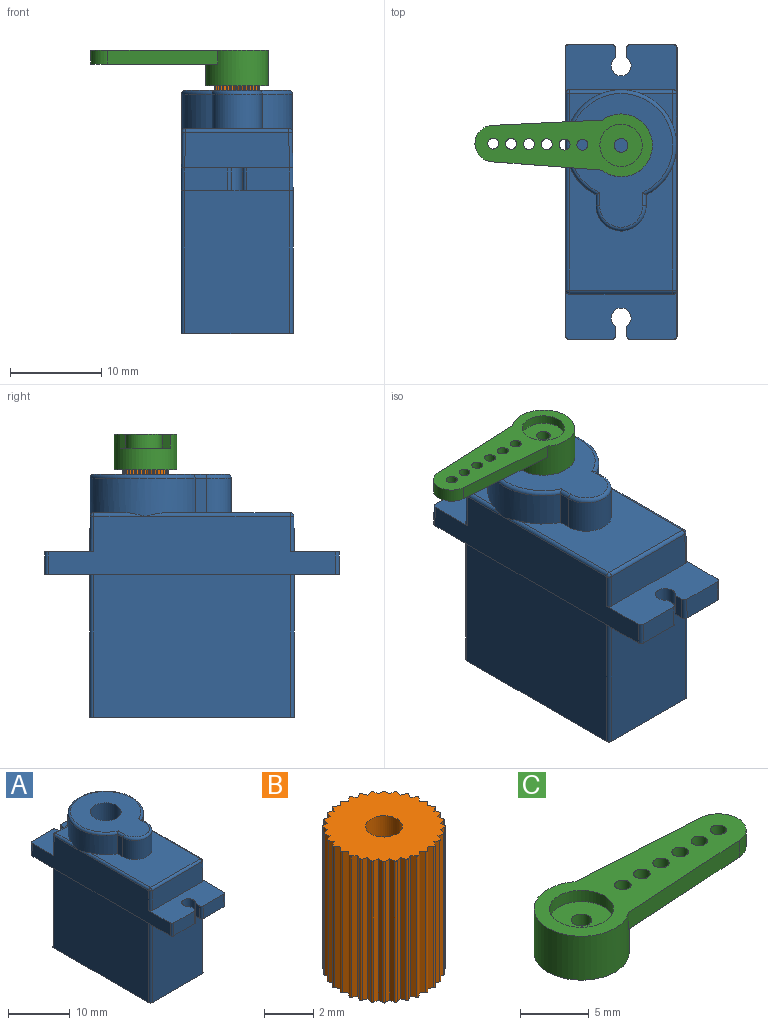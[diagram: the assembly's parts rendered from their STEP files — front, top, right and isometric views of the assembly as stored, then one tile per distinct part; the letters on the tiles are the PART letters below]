
ASSEMBLY  parts=3 mates=2
PART A: 64 faces, bbox 13.2x32.4x26.7 mm
  f0: plane 3.52x3.52mm, normal (0,0,1), area 4.4mm2, adj f4,f7,f57
  f1: plane 3.52x3.52mm, normal (0,0,1), area 4.4mm2, adj f5,f8,f57
  f2: plane 13.72x11.39mm, normal (0,0,1), area 107.7mm2, adj f3,f6,f47,f53,f54,f57,f58
  f3: cylinder r=0.4mm len=15.89mm, axis (0,1,0), area 9.3mm2, adj f2,f17,f45,f57
  f4: cylinder r=0.4mm len=5.69mm, axis (0,1,0), area 2.9mm2, adj f0,f17,f50,f57
  f5: cylinder r=0.4mm len=5.69mm, axis (0,1,0), area 2.9mm2, adj f1,f15,f51,f57
  f6: cylinder r=0.4mm len=15.89mm, axis (0,1,0), area 9.3mm2, adj f2,f15,f49,f57
  f7: cylinder r=0.4mm len=5.69mm, axis (-1,0,0), area 2.9mm2, adj f0,f16,f50,f57
  f8: cylinder r=0.4mm len=5.69mm, axis (-1,0,0), area 2.9mm2, adj f1,f16,f51,f57
  f9: plane 4.73x2.5mm, normal (0,1,0.01), area 11.8mm2, adj f11,f12,f32,f36
  f10: plane 4.73x2.5mm, normal (0,1,0.01), area 11.8mm2, adj f11,f12,f33,f37
  f11: plane 12.3x5.35mm, normal (0,0,-1), area 55.4mm2, adj f9,f10,f15,f17,f22,f29,f30,f31
  f12: plane 12.26x5.35mm, normal (0,0,1), area 55.2mm2, adj f9,f10,f15,f16,f17,f29,f30,f31
  f13: plane 4.73x2.5mm, normal (0,-1,0.01), area 11.8mm2, adj f14,f25,f34,f38
  f14: plane 12.26x5.35mm, normal (0,0,1), area 55.2mm2, adj f13,f15,f17,f18,f24,f26,f27,f28
  f15: plane 31.6x6.4mm, normal (1,0,0.01), area 163.4mm2, adj f5,f6,f11,f12,f14,f23,f25,f36
  f16: plane 11.46x3.9mm, normal (0,1,0.01), area 44.6mm2, adj f7,f8,f12,f48,f52
  f17: plane 31.6x6.4mm, normal (-1,0,0.01), area 163.4mm2, adj f3,f4,f11,f12,f14,f21,f25,f37
  f18: plane 11.46x3.9mm, normal (0,-1,0.01), area 44.6mm2, adj f14,f44,f46,f47
  f19: plane 22.5x12.3mm, normal (0,0,-1), area 276.6mm2, adj f20,f21,f22,f23,f40,f41,f42,f43
  f20: plane 15.7x11.5mm, normal (0,-1,0), area 180.5mm2, adj f19,f25,f42,f43
  f21: plane 21.7x15.7mm, normal (-1,0,0), area 340.7mm2, adj f17,f19,f41,f42
  f22: plane 15.7x11.5mm, normal (0,1,0), area 180.5mm2, adj f11,f19,f40,f41
  f23: plane 21.7x15.7mm, normal (1,0,0), area 340.7mm2, adj f15,f19,f40,f43
  f24: plane 4.73x2.5mm, normal (0,-1,0.01), area 11.8mm2, adj f14,f25,f35,f39
  f25: plane 12.3x5.35mm, normal (0,0,-1), area 55.4mm2, adj f13,f15,f17,f20,f24,f26,f27,f28
  f26: cylinder r=1.1mm len=2.5mm, axis (0,0,1), area 14mm2, adj f14,f25,f27,f28
  f27: plane 2.5x1.04mm, normal (1,0,0), area 2.6mm2, adj f14,f25,f26,f34
  f28: plane 2.5x1.04mm, normal (-1,0,0), area 2.6mm2, adj f14,f25,f26,f35
  f29: plane 2.5x1.04mm, normal (-1,0,0), area 2.6mm2, adj f11,f12,f31,f32
  f30: plane 2.5x1.04mm, normal (1,0,0), area 2.6mm2, adj f11,f12,f31,f33
  f31: cylinder r=1.1mm len=2.5mm, axis (0,0,1), area 14mm2, adj f11,f12,f29,f30
  f32: cylinder r=0.4mm len=2.51mm, axis (0,0.01,-1), area 1.6mm2, adj f9,f11,f12,f29
  f33: cylinder r=0.4mm len=2.51mm, axis (0,-0.01,1), area 1.6mm2, adj f10,f11,f12,f30
  f34: cylinder r=0.4mm len=2.51mm, axis (0,0.01,1), area 1.6mm2, adj f13,f14,f25,f27
  f35: cylinder r=0.4mm len=2.51mm, axis (0,-0.01,-1), area 1.6mm2, adj f14,f24,f25,f28
  f36: cylinder r=0.4mm len=2.5mm, axis (0.01,0.01,-1), area 1.6mm2, adj f9,f11,f12,f15
  f37: cylinder r=0.4mm len=2.5mm, axis (-0.01,0.01,-1), area 1.6mm2, adj f10,f11,f12,f17
  f38: cylinder r=0.4mm len=2.5mm, axis (-0.01,-0.01,-1), area 1.6mm2, adj f13,f14,f17,f25
  f39: cylinder r=0.4mm len=2.5mm, axis (0.01,-0.01,-1), area 1.6mm2, adj f14,f15,f24,f25
  f40: cylinder r=0.4mm len=15.7mm, axis (0,0,-1), area 9.9mm2, adj f11,f19,f22,f23
  f41: cylinder r=0.4mm len=15.7mm, axis (0,0,1), area 9.9mm2, adj f11,f19,f21,f22
  f42: cylinder r=0.4mm len=15.7mm, axis (0,0,-1), area 9.9mm2, adj f19,f20,f21,f25
  f43: cylinder r=0.4mm len=15.7mm, axis (0,0,1), area 9.9mm2, adj f19,f20,f23,f25
  f44: cylinder r=0.4mm len=3.91mm, axis (-0.01,-0.01,-1), area 2.5mm2, adj f14,f17,f18,f45
  f45: sphere r=0.4mm, area 0.2mm2, adj f3,f44,f47
  f46: cylinder r=0.4mm len=3.91mm, axis (0.01,-0.01,-1), area 2.5mm2, adj f14,f15,f18,f49
  f47: cylinder r=0.4mm len=11.39mm, axis (-1,0,0), area 7.1mm2, adj f2,f18,f45,f49
  f48: cylinder r=0.4mm len=3.91mm, axis (-0.01,0.01,-1), area 2.5mm2, adj f12,f16,f17,f50
  f49: sphere r=0.4mm, area 0.2mm2, adj f6,f46,f47
  f50: sphere r=0.4mm, area 0.2mm2, adj f4,f7,f48
  f51: sphere r=0.4mm, area 0.2mm2, adj f5,f8,f52
  f52: cylinder r=0.4mm len=3.91mm, axis (0.01,0.01,-1), area 2.5mm2, adj f12,f15,f16,f51
  f53: plane 3.8x1.22mm, normal (-1,0,0), area 4.6mm2, adj f2,f54,f57,f61
  f54: cylinder r=2.75mm len=5.5mm, axis (0,0,-1), area 32.8mm2, adj f2,f53,f58,f63
  f55: plane 14.7x11.39mm, normal (0,0,1), area 96.2mm2, adj f56,f60,f61,f62,f63
  f56: cylinder r=2.5mm len=5mm, axis (0,0,-1), area 66mm2, adj f55,f59
  f57: cylinder r=6.09mm len=12.19mm, axis (0,0,-1), area 125.9mm2, adj f0,f1,f2,f3,f4,f5,f6,f7
  f58: plane 3.8x1.22mm, normal (1,0,0), area 4.6mm2, adj f2,f54,f57,f62
  f59: plane 5x5mm, normal (0,0,1), area 19.6mm2, adj f56
  f60: torus R=5.69mm, axis (0,0,1), area 20.1mm2, adj f55,f57,f61,f62
  f61: cylinder r=0.4mm len=1.47mm, axis (0,1,0), area 0.8mm2, adj f53,f55,f60,f63
  f62: cylinder r=0.4mm len=1.47mm, axis (0,-1,0), area 0.8mm2, adj f55,f58,f60,f63
  f63: torus R=2.35mm, axis (0,0,1), area 5.1mm2, adj f54,f55,f61,f62
PART B: 99 faces, bbox 5x5x7.1 mm
  f0: plane 5x5mm, normal (0,0,-1), area 16.5mm2, adj f1,f2,f3,f4,f5,f6,f7,f8
  f1: plane 7.05x0.2mm, normal (-0.8,0.6,0), area 1.7mm2, adj f0,f2,f94,f95
  f2: cylinder r=0.08mm len=7.05mm, axis (0,0,-1), area 0.9mm2, adj f0,f1,f3,f94
  f3: plane 7.05x0.21mm, normal (-0.51,-0.86,0), area 1.7mm2, adj f0,f2,f4,f94
  f4: plane 7.05x0.22mm, normal (-0.9,0.43,0), area 1.7mm2, adj f0,f3,f5,f94
  f5: cylinder r=0.08mm len=7.05mm, axis (0,0,-1), area 0.9mm2, adj f0,f4,f6,f94
  f6: plane 7.05x0.23mm, normal (-0.33,-0.94,0), area 1.7mm2, adj f0,f5,f7,f94
  f7: plane 7.05x0.24mm, normal (-0.97,0.25,0), area 1.7mm2, adj f0,f6,f8,f94
  f8: cylinder r=0.08mm len=7.05mm, axis (0,0,-1), area 0.9mm2, adj f0,f7,f9,f94
  f9: plane 7.05x0.25mm, normal (-0.14,-0.99,0), area 1.7mm2, adj f0,f8,f10,f94
  f10: plane 7.05x0.25mm, normal (-1,0.05,0), area 1.7mm2, adj f0,f9,f11,f94
  f11: cylinder r=0.08mm len=7.05mm, axis (0,0,-1), area 0.9mm2, adj f0,f10,f12,f94
  f12: plane 7.05x0.25mm, normal (0.05,-1,0), area 1.7mm2, adj f0,f11,f13,f94
  f13: plane 7.05x0.25mm, normal (-0.99,-0.14,0), area 1.7mm2, adj f0,f12,f14,f94
  f14: cylinder r=0.08mm len=7.05mm, axis (0,0,-1), area 0.9mm2, adj f0,f13,f15,f94
  f15: plane 7.05x0.24mm, normal (0.25,-0.97,0), area 1.7mm2, adj f0,f14,f16,f94
  f16: plane 7.05x0.23mm, normal (-0.94,-0.33,0), area 1.7mm2, adj f0,f15,f17,f94
  f17: cylinder r=0.08mm len=7.05mm, axis (0,0,-1), area 0.9mm2, adj f0,f16,f18,f94
  f18: plane 7.05x0.22mm, normal (0.43,-0.9,0), area 1.7mm2, adj f0,f17,f19,f94
  f19: plane 7.05x0.21mm, normal (-0.86,-0.51,0), area 1.7mm2, adj f0,f18,f20,f94
  f20: cylinder r=0.08mm len=7.05mm, axis (0,0,-1), area 0.9mm2, adj f0,f19,f21,f94
  f21: plane 7.05x0.2mm, normal (0.6,-0.8,0), area 1.7mm2, adj f0,f20,f22,f94
  f22: plane 7.05x0.18mm, normal (-0.74,-0.67,0), area 1.7mm2, adj f0,f21,f23,f94
  f23: cylinder r=0.08mm len=7.05mm, axis (0,0,-1), area 0.9mm2, adj f0,f22,f24,f94
  f24: plane 7.05x0.18mm, normal (0.74,-0.67,0), area 1.7mm2, adj f0,f23,f25,f94
  f25: plane 7.05x0.2mm, normal (-0.6,-0.8,0), area 1.7mm2, adj f0,f24,f26,f94
  f26: cylinder r=0.08mm len=7.05mm, axis (0,0,-1), area 0.9mm2, adj f0,f25,f27,f94
  f27: plane 7.05x0.21mm, normal (0.86,-0.51,0), area 1.7mm2, adj f0,f26,f28,f94
  f28: plane 7.05x0.22mm, normal (-0.43,-0.9,0), area 1.7mm2, adj f0,f27,f29,f94
  f29: cylinder r=0.08mm len=7.05mm, axis (0,0,-1), area 0.9mm2, adj f0,f28,f30,f94
  f30: plane 7.05x0.23mm, normal (0.94,-0.33,0), area 1.7mm2, adj f0,f29,f31,f94
  f31: plane 7.05x0.24mm, normal (-0.25,-0.97,0), area 1.7mm2, adj f0,f30,f32,f94
  f32: cylinder r=0.08mm len=7.05mm, axis (0,0,-1), area 0.9mm2, adj f0,f31,f33,f94
  f33: plane 7.05x0.25mm, normal (0.99,-0.14,0), area 1.7mm2, adj f0,f32,f34,f94
  f34: plane 7.05x0.25mm, normal (-0.05,-1,0), area 1.7mm2, adj f0,f33,f35,f94
  f35: cylinder r=0.08mm len=7.05mm, axis (0,0,-1), area 0.9mm2, adj f0,f34,f36,f94
  f36: plane 7.05x0.25mm, normal (1,0.05,0), area 1.7mm2, adj f0,f35,f37,f94
  f37: plane 7.05x0.25mm, normal (0.14,-0.99,0), area 1.7mm2, adj f0,f36,f38,f94
  f38: cylinder r=0.08mm len=7.05mm, axis (0,0,-1), area 0.9mm2, adj f0,f37,f39,f94
  f39: plane 7.05x0.24mm, normal (0.97,0.25,0), area 1.7mm2, adj f0,f38,f40,f94
  f40: plane 7.05x0.23mm, normal (0.33,-0.94,0), area 1.7mm2, adj f0,f39,f41,f94
  f41: cylinder r=0.08mm len=7.05mm, axis (0,0,-1), area 0.9mm2, adj f0,f40,f42,f94
  f42: plane 7.05x0.22mm, normal (0.9,0.43,0), area 1.7mm2, adj f0,f41,f43,f94
  f43: plane 7.05x0.21mm, normal (0.51,-0.86,0), area 1.7mm2, adj f0,f42,f44,f94
  f44: cylinder r=0.08mm len=7.05mm, axis (0,0,-1), area 0.9mm2, adj f0,f43,f45,f94
  f45: plane 7.05x0.2mm, normal (0.8,0.6,0), area 1.7mm2, adj f0,f44,f46,f94
  f46: plane 7.05x0.18mm, normal (0.67,-0.74,0), area 1.7mm2, adj f0,f45,f47,f94
  f47: cylinder r=0.08mm len=7.05mm, axis (0,0,-1), area 0.9mm2, adj f0,f46,f48,f94
  f48: plane 7.05x0.18mm, normal (0.67,0.74,0), area 1.7mm2, adj f0,f47,f49,f94
  f49: plane 7.05x0.2mm, normal (0.8,-0.6,0), area 1.7mm2, adj f0,f48,f50,f94
  f50: cylinder r=0.08mm len=7.05mm, axis (0,0,-1), area 0.9mm2, adj f0,f49,f51,f94
  f51: plane 7.05x0.21mm, normal (0.51,0.86,0), area 1.7mm2, adj f0,f50,f52,f94
  f52: plane 7.05x0.22mm, normal (0.9,-0.43,0), area 1.7mm2, adj f0,f51,f53,f94
  f53: cylinder r=0.08mm len=7.05mm, axis (0,0,-1), area 0.9mm2, adj f0,f52,f54,f94
  f54: plane 7.05x0.23mm, normal (0.33,0.94,0), area 1.7mm2, adj f0,f53,f55,f94
  f55: plane 7.05x0.24mm, normal (0.97,-0.25,0), area 1.7mm2, adj f0,f54,f56,f94
  f56: cylinder r=0.08mm len=7.05mm, axis (0,0,-1), area 0.9mm2, adj f0,f55,f57,f94
  f57: plane 7.05x0.25mm, normal (0.14,0.99,0), area 1.7mm2, adj f0,f56,f58,f94
  f58: plane 7.05x0.25mm, normal (1,-0.05,0), area 1.7mm2, adj f0,f57,f59,f94
  f59: cylinder r=0.08mm len=7.05mm, axis (0,0,-1), area 0.9mm2, adj f0,f58,f60,f94
  f60: plane 7.05x0.25mm, normal (-0.05,1,0), area 1.7mm2, adj f0,f59,f61,f94
  f61: plane 7.05x0.25mm, normal (0.99,0.14,0), area 1.7mm2, adj f0,f60,f62,f94
  f62: cylinder r=0.08mm len=7.05mm, axis (0,0,-1), area 0.9mm2, adj f0,f61,f63,f94
  f63: plane 7.05x0.24mm, normal (-0.25,0.97,0), area 1.7mm2, adj f0,f62,f64,f94
  f64: plane 7.05x0.23mm, normal (0.94,0.33,0), area 1.7mm2, adj f0,f63,f65,f94
  f65: cylinder r=0.08mm len=7.05mm, axis (0,0,-1), area 0.9mm2, adj f0,f64,f66,f94
  f66: plane 7.05x0.22mm, normal (-0.43,0.9,0), area 1.7mm2, adj f0,f65,f67,f94
  f67: plane 7.05x0.21mm, normal (0.86,0.51,0), area 1.7mm2, adj f0,f66,f68,f94
  f68: cylinder r=0.08mm len=7.05mm, axis (0,0,-1), area 0.9mm2, adj f0,f67,f69,f94
  f69: plane 7.05x0.2mm, normal (-0.6,0.8,0), area 1.7mm2, adj f0,f68,f70,f94
  f70: plane 7.05x0.18mm, normal (0.74,0.67,0), area 1.7mm2, adj f0,f69,f71,f94
  f71: cylinder r=0.08mm len=7.05mm, axis (0,0,-1), area 0.9mm2, adj f0,f70,f72,f94
  f72: plane 7.05x0.18mm, normal (-0.74,0.67,0), area 1.7mm2, adj f0,f71,f73,f94
  f73: plane 7.05x0.2mm, normal (0.6,0.8,0), area 1.7mm2, adj f0,f72,f74,f94
  f74: cylinder r=0.08mm len=7.05mm, axis (0,0,-1), area 0.9mm2, adj f0,f73,f75,f94
  f75: plane 7.05x0.21mm, normal (-0.86,0.51,0), area 1.7mm2, adj f0,f74,f76,f94
  f76: plane 7.05x0.22mm, normal (0.43,0.9,0), area 1.7mm2, adj f0,f75,f77,f94
  f77: cylinder r=0.08mm len=7.05mm, axis (0,0,-1), area 0.9mm2, adj f0,f76,f78,f94
  f78: plane 7.05x0.23mm, normal (-0.94,0.33,0), area 1.7mm2, adj f0,f77,f79,f94
  f79: plane 7.05x0.24mm, normal (0.25,0.97,0), area 1.7mm2, adj f0,f78,f80,f94
  f80: cylinder r=0.08mm len=7.05mm, axis (0,0,-1), area 0.9mm2, adj f0,f79,f81,f94
  f81: plane 7.05x0.25mm, normal (-0.99,0.14,0), area 1.7mm2, adj f0,f80,f82,f94
  f82: plane 7.05x0.25mm, normal (0.05,1,0), area 1.7mm2, adj f0,f81,f83,f94
  f83: cylinder r=0.08mm len=7.05mm, axis (0,0,-1), area 0.9mm2, adj f0,f82,f84,f94
  f84: plane 7.05x0.25mm, normal (-1,-0.05,0), area 1.7mm2, adj f0,f83,f85,f94
  f85: plane 7.05x0.25mm, normal (-0.14,0.99,0), area 1.7mm2, adj f0,f84,f86,f94
  f86: cylinder r=0.08mm len=7.05mm, axis (0,0,-1), area 0.9mm2, adj f0,f85,f87,f94
  f87: plane 7.05x0.24mm, normal (-0.97,-0.25,0), area 1.7mm2, adj f0,f86,f88,f94
  f88: plane 7.05x0.23mm, normal (-0.33,0.94,0), area 1.7mm2, adj f0,f87,f89,f94
  f89: cylinder r=0.08mm len=7.05mm, axis (0,0,-1), area 0.9mm2, adj f0,f88,f90,f94
  f90: plane 7.05x0.22mm, normal (-0.9,-0.43,0), area 1.7mm2, adj f0,f89,f91,f94
  f91: plane 7.05x0.21mm, normal (-0.51,0.86,0), area 1.7mm2, adj f0,f90,f92,f94
  f92: cylinder r=0.08mm len=7.05mm, axis (0,0,-1), area 0.9mm2, adj f0,f91,f93,f94
  f93: plane 7.05x0.2mm, normal (-0.8,-0.6,0), area 1.7mm2, adj f0,f92,f94,f96
  f94: plane 5x5mm, normal (0,0,1), area 16.5mm2, adj f1,f2,f3,f4,f5,f6,f7,f8
  f95: plane 7.05x0.18mm, normal (-0.67,-0.74,0), area 1.7mm2, adj f0,f1,f94,f97
  f96: plane 7.05x0.18mm, normal (-0.67,0.74,0), area 1.7mm2, adj f0,f93,f94,f97
  f97: cylinder r=0.08mm len=7.05mm, axis (0,0,-1), area 0.9mm2, adj f0,f94,f95,f96
  f98: cylinder r=0.75mm len=7.05mm, axis (0,0,-1), area 33.2mm2, adj f0,f94
PART C: 18 faces, bbox 19.5x6.9x3.9 mm
  f0: plane 4.65x4.65mm, normal (0,0,1), area 15.2mm2, adj f1,f7
  f1: cylinder r=0.75mm len=1.5mm, axis (0,0,-1), area 4.9mm2, adj f0,f2
  f2: plane 5x5mm, normal (0,0,-1), area 17.9mm2, adj f1,f3
  f3: cylinder r=2.5mm len=5mm, axis (0,0,-1), area 29.1mm2, adj f2,f4
  f4: plane 6.9x6.9mm, normal (0,0,-1), area 17.8mm2, adj f3,f5
  f5: cylinder r=3.45mm len=6.9mm, axis (0,0,-1), area 75mm2, adj f4,f6,f8,f9,f11
  f6: plane 19.5x6.9mm, normal (0,0,1), area 71.6mm2, adj f5,f7,f8,f9,f10,f12,f13,f14
  f7: cylinder r=2.32mm len=4.65mm, axis (0,0,-1), area 14.6mm2, adj f0,f6
  f8: plane 12.09x1.5mm, normal (0.06,1,0), area 18.2mm2, adj f5,f6,f10,f11
  f9: plane 12.09x1.5mm, normal (0.06,-1,0), area 18.2mm2, adj f5,f6,f10,f11
  f10: cylinder r=2mm len=4mm, axis (0,0,1), area 9.1mm2, adj f6,f8,f9,f11
  f11: plane 13.97x5.5mm, normal (0,0,-1), area 51.2mm2, adj f5,f8,f9,f10,f12,f13,f14,f15
  f12: cylinder r=0.6mm len=1.5mm, axis (0,0,1), area 5.7mm2, adj f6,f11
  f13: cylinder r=0.6mm len=1.5mm, axis (0,0,1), area 5.7mm2, adj f6,f11
  f14: cylinder r=0.6mm len=1.5mm, axis (0,0,1), area 5.7mm2, adj f6,f11
  f15: cylinder r=0.6mm len=1.5mm, axis (0,0,1), area 5.7mm2, adj f6,f11
  f16: cylinder r=0.6mm len=1.5mm, axis (0,0,1), area 5.7mm2, adj f6,f11
  f17: cylinder r=0.6mm len=1.5mm, axis (0,0,1), area 5.7mm2, adj f6,f11
PLACE A t=(-8.57,-5.89,-5.79)mm fixed
PLACE B rot(axis=(0.44,-0.9,0),180deg) t=(-4.52,-3.88,13.43)mm
PLACE C rot(axis=(0,0,1),179.2deg) t=(-8.5,4.31,-6.29)mm
MATE revolute C.f1 <-> B.f98  axis (0,0,-1) through (-8.57,-0.79,6.63)mm
MATE revolute B.f98 <-> A.f56  axis (0,0,1) through (-8.57,-0.79,3.11)mm
